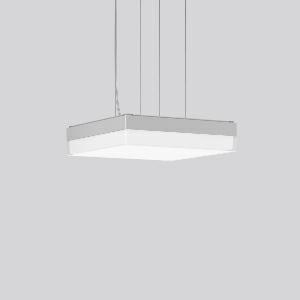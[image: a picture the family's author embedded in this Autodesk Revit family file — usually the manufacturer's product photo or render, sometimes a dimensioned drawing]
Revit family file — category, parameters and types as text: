
# Revit family: flat_slim_square_312542_004_76_9d9a
name_source: partatom
category: Lighting Fixtures
units: mm (PartAtom-declared; Revit-internal decimal feet)

## family parameters
Cut with Voids When Loaded = No
Host = Face
Light Source = No
Part Type = Normal
Room Calculation Point = No
Round Connector Dimension = Use Diameter
Shared = No

## types (1)
- MultiLumen 2 840 (1 x LED Modul 840, 2300 lm, 4000)
    Apparent Load = 21 VA
    CIE Flux Codes = 43 75 93 91 100
    Color Rendering = 80
    Color Temperature = 4000
    Default Elevation = 1800 mm
    Height = 70 mm
    Lamp = 1 x LED Modul 840
    Lamp Light Flux = 2300 lm
    Lamp count = 1
    Length = 300 mm
    Lifetime = 50000 h
    Luminous efficacy = 110 lm/W
    Manufacturer = RZB
    ModVariant = No
    Model = 312542.004.76
    Mounting Place = Ceiling
    Mounting Type = Pendant
    Number of Poles = 1
    OnlyDefault = Yes
    Power Factor = 1
    Product Name = FLAT SLIM square
    Product group = Pendant luminaires
    ProductGroupID = 902
    Protection Class = Protection class I
    Protection Degree = IP 40
    RLX_Detail_Level = 1
    RLX_Emergency_Light_Flux = 0 lm
    RLX_Emergency_Type = 0
    RLX_Emergency_Type_DB = No
    RlxData = <blob elided: 14333 chars, md5=d33313a2>
    Socket = socket
    Standby Power = 0 W
    System Light Flux = 2300 lm
    System Power = 21 W
    Type Comments = MultiLumen 2 840
    Type Image = 312542.004.jpg
    URL = http://relux.com
    VarID = multilumen_2_840
    Voltage = 230 V
    Voltage Range = 220-240 V
    Weight = 0.00 kg
    Width = 300 mm

## geometry (parser evidence)
native form markers: Sweep x16
no freeform markers — native parametric forms only
